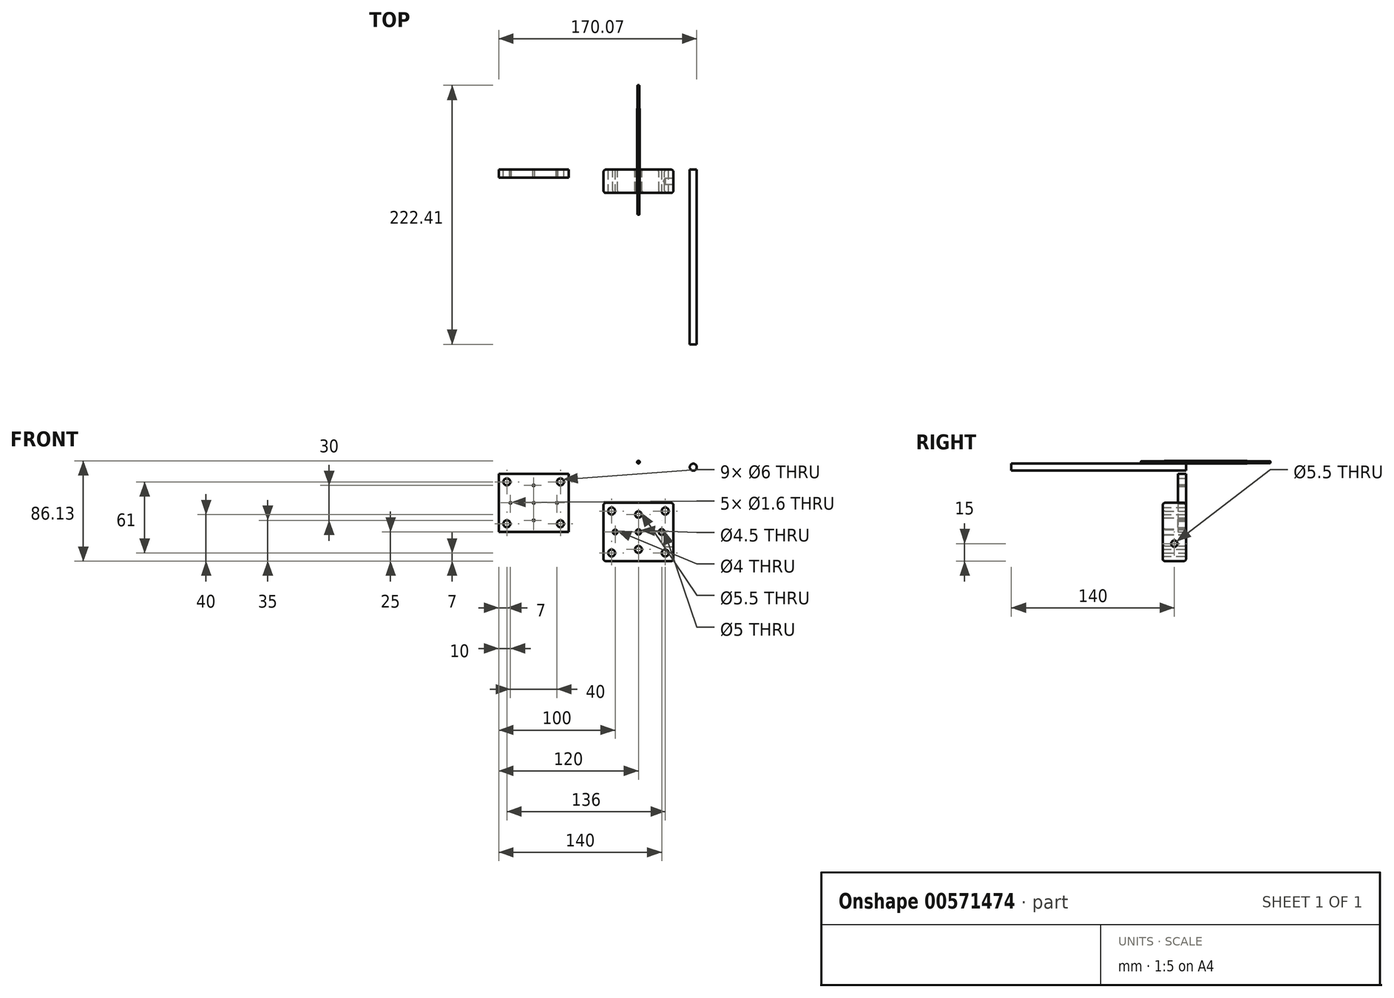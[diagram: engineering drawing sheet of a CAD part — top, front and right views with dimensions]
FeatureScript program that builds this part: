
annotation { "Feature Type Name" : "Feature", "Feature Type Description" : "" }
export const myFeature = defineFeature(function(context is Context, id is Id, definition is map)
    precondition{}
    {
        {
            var Q0;
            Q0=qCreatedBy(makeId("Front.planeOp"),FACE);
            var sketch = newSketch(context, id + "F0", { "sketchPlane" : qUnion([Q0])});
            skLineSegment(sketch, "E0.bottom", {"start": v(-30, 25) * mm, "end": v(30, 25) * mm});
            skLineSegment(sketch, "E0.top", {"start": v(-30, -25) * mm, "end": v(30, -25) * mm});
            skLineSegment(sketch, "E0.left", {"start": v(-30, 25) * mm, "end": v(-30, -25) * mm});
            skLineSegment(sketch, "E0.right", {"start": v(30, 25) * mm, "end": v(30, -25) * mm});
            skPoint(sketch, "E0.middle", {"position": v(0, 0) * mm});
            skCircle(sketch, "E1", {"center": v(-23, 18) * mm, "radius": 3 * mm});
            skCircle(sketch, "E2", {"center": v(-23, -18) * mm, "radius": 3 * mm});
            skCircle(sketch, "E3", {"center": v(23, -18) * mm, "radius": 3 * mm});
            skCircle(sketch, "E4", {"center": v(23, 18) * mm, "radius": 3 * mm});
            skCircle(sketch, "E5", {"center": v(0, 0) * mm, "radius": 2.25 * mm});
            skCircle(sketch, "E6", {"center": v(-20, 0) * mm, "radius": 2 * mm});
            skCircle(sketch, "E7", {"center": v(0, 15) * mm, "radius": 2.75 * mm});
            skCircle(sketch, "E8", {"center": v(0, -15) * mm, "radius": 3 * mm});
            skCircle(sketch, "E9", {"center": v(20, 0) * mm, "radius": 2.5 * mm});
            skSolve(sketch);
        }
        {
            var Q0;
            Q0=makeQuery(id+"F0.imprint","IMPRINT",FACE,{"disambiguationData":[TD([[makeQuery(id+"F0.imprint","IMPRINT",EDGE,{"derivedFrom":sQuery(id+"F0.wireOp",EDGE,"E0.bottom")}),-1.0]])]});
            extrude(context, id + "F1", {"entities" : qUnion([Q0]), "depth" : 20 * mm, "offsetDistance" : 25 * mm});
        }
        {
            var Q0;
            Q0=makeQuery(id+"F1.opExtrude","SWEPT_FACE",FACE,{"disambiguationData":[OSD([sQuery(id+"F0.wireOp",EDGE,"E0.right")])]});
            var sketch = newSketch(context, id + "F2", { "sketchPlane" : qUnion([Q0])});
            skCircle(sketch, "E10", {"center": v(-10, -10) * mm, "radius": 1.33 * mm});
            skSolve(sketch);
        }
        {
            var Q0;
            Q0=sQuery(id+"F2.wireOp",VERTEX,"E10.center");
            var Q1;
            Q1=makeQuery(id+"F1.opExtrude","SWEPT_BODY",BODY,{"disambiguationData":[OSD([sQuery(id+"F0.wireOp",EDGE,"E0.bottom"),sQuery(id+"F0.wireOp",EDGE,"E0.top"),sQuery(id+"F0.wireOp",EDGE,"E0.left"),sQuery(id+"F0.wireOp",EDGE,"E0.right"),sQuery(id+"F0.wireOp",EDGE,"E1"),sQuery(id+"F0.wireOp",EDGE,"E2"),sQuery(id+"F0.wireOp",EDGE,"E3"),sQuery(id+"F0.wireOp",EDGE,"E4"),sQuery(id+"F0.wireOp",EDGE,"E5"),sQuery(id+"F0.wireOp",EDGE,"E6"),sQuery(id+"F0.wireOp",EDGE,"E7"),sQuery(id+"F0.wireOp",EDGE,"E8"),sQuery(id+"F0.wireOp",EDGE,"E9")])]});
            hole(context, id + "F3", {"style" : HoleStyle.SIMPLE, "endStyle" : HoleEndStyle.BLIND, "standardTappedOrClearance" : lookupTablePath({ "standard" : "ISO", "fit" : "Normal", "size" : "M5", "type" : "Clearance" }), "standardBlindInLast" : lookupTablePath({ "fit" : "Standard", "standard" : "ISO", "size" : "M5", "type" : "Clearance" }), "holeDiameter" : 5.5 * mm, "holeDepth" : 7 * mm, "isTappedThrough" : true, "tappedDepth" : 12 * mm, "tapClearance" : 3, "locations" : qUnion([Q0]), "scope" : qUnion([Q1])});
        }
        {
            var Q0;
            Q0=makeQuery(id+"F1.opExtrude","CAP_EDGE",EDGE,{"disambiguationData":[OSD([sQuery(id+"F0.wireOp",EDGE,"E0.bottom")])],"isStart":false});
            var Q1;
            Q1=makeQuery(id+"F1.opExtrude","CAP_EDGE",EDGE,{"disambiguationData":[OSD([sQuery(id+"F0.wireOp",EDGE,"E0.bottom")])],"isStart":true});
            var Q2;
            Q2=makeQuery(id+"F1.opExtrude","SWEPT_EDGE",EDGE,{"disambiguationData":[OSD([sQuery(id+"F0.wireOp",EDGE,"E0.bottom"),sQuery(id+"F0.wireOp",EDGE,"E0.left")])]});
            var Q3;
            Q3=makeQuery(id+"F1.opExtrude","CAP_EDGE",EDGE,{"disambiguationData":[OSD([sQuery(id+"F0.wireOp",EDGE,"E0.left")])],"isStart":false});
            var Q4;
            Q4=makeQuery(id+"F1.opExtrude","CAP_EDGE",EDGE,{"disambiguationData":[OSD([sQuery(id+"F0.wireOp",EDGE,"E0.left")])],"isStart":true});
            var Q5;
            Q5=makeQuery(id+"F1.opExtrude","SWEPT_EDGE",EDGE,{"disambiguationData":[OSD([sQuery(id+"F0.wireOp",EDGE,"E0.bottom"),sQuery(id+"F0.wireOp",EDGE,"E0.right")])]});
            var Q6;
            Q6=makeQuery(id+"F1.opExtrude","CAP_EDGE",EDGE,{"disambiguationData":[OSD([sQuery(id+"F0.wireOp",EDGE,"E0.right")])],"isStart":true});
            var Q7;
            Q7=makeQuery(id+"F1.opExtrude","CAP_EDGE",EDGE,{"disambiguationData":[OSD([sQuery(id+"F0.wireOp",EDGE,"E0.right")])],"isStart":false});
            var Q8;
            Q8=makeQuery(id+"F1.opExtrude","SWEPT_EDGE",EDGE,{"disambiguationData":[OSD([sQuery(id+"F0.wireOp",EDGE,"E0.top"),sQuery(id+"F0.wireOp",EDGE,"E0.right")])]});
            var Q9;
            Q9=makeQuery(id+"F1.opExtrude","CAP_EDGE",EDGE,{"disambiguationData":[OSD([sQuery(id+"F0.wireOp",EDGE,"E0.top")])],"isStart":false});
            var Q10;
            Q10=makeQuery(id+"F1.opExtrude","CAP_EDGE",EDGE,{"disambiguationData":[OSD([sQuery(id+"F0.wireOp",EDGE,"E0.top")])],"isStart":true});
            fillet(context, id + "F4", {"entities" : qUnion([Q0, Q1, Q2, Q3, Q4, Q5, Q6, Q7, Q8, Q9, Q10]), "radius" : 2 * mm, "tangentPropagation" : true, "allowEdgeOverflow" : false});
        }
        {
            var Q0;
            Q0=makeQuery(id+"F1.opExtrude","CAP_EDGE",EDGE,{"disambiguationData":[OSD([sQuery(id+"F0.wireOp",EDGE,"E8")])],"isStart":false});
            var Q1;
            Q1=makeQuery(id+"F1.opExtrude","CAP_EDGE",EDGE,{"disambiguationData":[OSD([sQuery(id+"F0.wireOp",EDGE,"E6")])],"isStart":false});
            var Q2;
            Q2=makeQuery(id+"F1.opExtrude","CAP_EDGE",EDGE,{"disambiguationData":[OSD([sQuery(id+"F0.wireOp",EDGE,"E7")])],"isStart":false});
            var Q3;
            Q3=makeQuery(id+"F1.opExtrude","CAP_EDGE",EDGE,{"disambiguationData":[OSD([sQuery(id+"F0.wireOp",EDGE,"E5")])],"isStart":false});
            var Q4;
            Q4=makeQuery(id+"F1.opExtrude","CAP_EDGE",EDGE,{"disambiguationData":[OSD([sQuery(id+"F0.wireOp",EDGE,"E9")])],"isStart":false});
            var Q5;
            Q5=makeQuery(id+"F1.opExtrude","CAP_EDGE",EDGE,{"disambiguationData":[OSD([sQuery(id+"F0.wireOp",EDGE,"E8")])],"isStart":true});
            var Q6;
            Q6=makeQuery(id+"F1.opExtrude","CAP_EDGE",EDGE,{"disambiguationData":[OSD([sQuery(id+"F0.wireOp",EDGE,"E9")])],"isStart":true});
            var Q7;
            Q7=makeQuery(id+"F1.opExtrude","CAP_EDGE",EDGE,{"disambiguationData":[OSD([sQuery(id+"F0.wireOp",EDGE,"E6")])],"isStart":true});
            var Q8;
            Q8=makeQuery(id+"F1.opExtrude","CAP_EDGE",EDGE,{"disambiguationData":[OSD([sQuery(id+"F0.wireOp",EDGE,"E7")])],"isStart":true});
            fillet(context, id + "F5", {"entities" : qUnion([Q0, Q1, Q2, Q3, Q4, Q5, Q6, Q7, Q8]), "radius" : 2 * mm, "tangentPropagation" : true, "allowEdgeOverflow" : false});
        }
        {
            var Q0;
            Q0=makeQuery(id+"F1.opExtrude","CAP_EDGE",EDGE,{"disambiguationData":[OSD([sQuery(id+"F0.wireOp",EDGE,"E5")])],"isStart":true});
            fillet(context, id + "F6", {"entities" : qUnion([Q0]), "radius" : 2 * mm, "tangentPropagation" : true, "allowEdgeOverflow" : false});
        }
        {
            var Q0;
            Q0=makeQuery(id+"F1.opExtrude","SWEPT_EDGE",EDGE,{"disambiguationData":[OSD([sQuery(id+"F0.wireOp",EDGE,"E0.top"),sQuery(id+"F0.wireOp",EDGE,"E0.left")])]});
            fillet(context, id + "F7", {"entities" : qUnion([Q0]), "radius" : 2 * mm, "tangentPropagation" : true, "allowEdgeOverflow" : false});
        }
        {
            var Q0;
            Q0=qCreatedBy(makeId("Right.planeOp"),FACE);
            var sketch = newSketch(context, id + "F8", { "sketchPlane" : qUnion([Q0])});
            skLineSegment(sketch, "E11", {"start": v(72.41, 60) * mm, "end": v(-38.59, 60) * mm});
            skLineSegment(sketch, "E12", {"start": v(72.41, 60) * mm, "end": v(72.41, 59.2) * mm});
            skLineSegment(sketch, "E13", {"start": v(72.41, 59.2) * mm, "end": v(52.41, 59.2) * mm});
            skLineSegment(sketch, "E14", {"start": v(52.41, 59.2) * mm, "end": v(52.41, 58.88) * mm});
            skLineSegment(sketch, "E15", {"start": v(52.41, 58.88) * mm, "end": v(-18.59, 58.87) * mm});
            skLineSegment(sketch, "E16", {"start": v(-18.59, 58.87) * mm, "end": v(-18.59, 59.2) * mm});
            skLineSegment(sketch, "E17", {"start": v(-18.59, 59.2) * mm, "end": v(-38.59, 59.2) * mm});
            skLineSegment(sketch, "E18", {"start": v(-38.59, 60) * mm, "end": v(-38.59, 59.2) * mm});
            skSolve(sketch);
        }
        {
            var Q0;
            Q0=makeQuery(id+"F8.imprint","IMPRINT",FACE,{"disambiguationData":[TD([[makeQuery(id+"F8.imprint","IMPRINT",EDGE,{"derivedFrom":sQuery(id+"F8.wireOp",EDGE,"E11")}),1.0]])]});
            var Q1;
            Q1=sQuery(id+"F8.wireOp",EDGE,"E11");
            revolve(context, id + "F9", {"entities" : qUnion([Q0]), "axis" : qUnion([Q1]), "revolveType" : RevolveType.FULL});
        }
        {
            var Q0;
            Q0=qCreatedBy(makeId("Front.planeOp"),FACE);
            var sketch = newSketch(context, id + "F10", { "sketchPlane" : qUnion([Q0])});
            skLineSegment(sketch, "E19.bottom", {"start": v(-60, 50) * mm, "end": v(-120, 50) * mm});
            skLineSegment(sketch, "E19.top", {"start": v(-60, 0) * mm, "end": v(-120, 0) * mm});
            skLineSegment(sketch, "E19.left", {"start": v(-60, 50) * mm, "end": v(-60, 0) * mm});
            skLineSegment(sketch, "E19.right", {"start": v(-120, 50) * mm, "end": v(-120, 0) * mm});
            skCircle(sketch, "E20", {"center": v(-67, 43) * mm, "radius": 3 * mm});
            skCircle(sketch, "E21", {"center": v(-113, 43) * mm, "radius": 3 * mm});
            skCircle(sketch, "E22", {"center": v(-113, 7) * mm, "radius": 3 * mm});
            skCircle(sketch, "E23", {"center": v(-67, 7) * mm, "radius": 3 * mm});
            skCircle(sketch, "E24", {"center": v(-90, 25) * mm, "radius": 0.8 * mm});
            skCircle(sketch, "E25", {"center": v(-70, 25) * mm, "radius": 0.8 * mm});
            skCircle(sketch, "E26", {"center": v(-110, 25) * mm, "radius": 0.8 * mm});
            skCircle(sketch, "E27", {"center": v(-90, 40) * mm, "radius": 0.8 * mm});
            skCircle(sketch, "E28", {"center": v(-90, 10) * mm, "radius": 0.8 * mm});
            skSolve(sketch);
        }
        {
            var Q0;
            Q0=makeQuery(id+"F10.imprint","IMPRINT",FACE,{"disambiguationData":[TD([[makeQuery(id+"F10.imprint","IMPRINT",EDGE,{"derivedFrom":sQuery(id+"F10.wireOp",EDGE,"E19.bottom")}),1.0]])]});
            extrude(context, id + "F11", {"entities" : qUnion([Q0]), "depth" : 7 * mm, "offsetDistance" : 25 * mm});
        }
        {
            var Q0;
            Q0=qCreatedBy(makeId("Front.planeOp"),FACE);
            var sketch = newSketch(context, id + "F12", { "sketchPlane" : qUnion([Q0])});
            skCircle(sketch, "E29", {"center": v(47.07, 55.69) * mm, "radius": 3 * mm});
            skSolve(sketch);
        }
        {
            var Q0;
            Q0=makeQuery(id+"F12.imprint","IMPRINT",FACE,{"disambiguationData":[TD([[makeQuery(id+"F12.imprint","IMPRINT",EDGE,{"derivedFrom":sQuery(id+"F12.wireOp",EDGE,"E29")}),1.0]])]});
            extrude(context, id + "F13", {"entities" : qUnion([Q0]), "depth" : 150 * mm, "offsetDistance" : 25 * mm});
        }
    });
